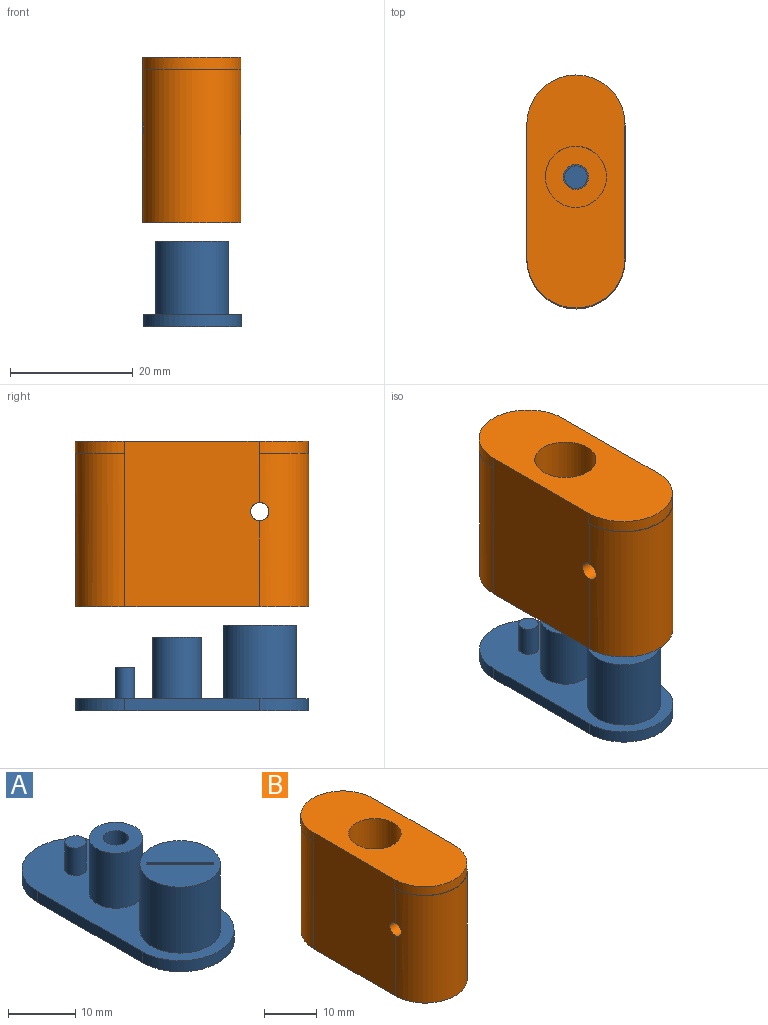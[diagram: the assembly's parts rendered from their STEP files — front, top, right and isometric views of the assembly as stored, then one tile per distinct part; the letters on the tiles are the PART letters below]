
ASSEMBLY  parts=2 mates=1
PART A: 19 faces, bbox 16x38x14 mm
  f0: plane 12x0.35mm, normal (0.71,-0.71,0), area 6mm2, adj f1,f4,f5,f6
  f1: plane 12x7.07mm, normal (-0.71,-0.71,0), area 120mm2, adj f0,f2,f5,f6
  f2: plane 12x0.35mm, normal (-0.71,0.71,0), area 6mm2, adj f1,f4,f5,f6
  f3: cylinder r=6mm len=12mm, axis (0,0,-1), area 452.4mm2, adj f5,f7
  f4: plane 12x7.07mm, normal (0.71,0.71,0), area 120mm2, adj f0,f2,f5,f6
  f5: plane 12x12mm, normal (0,0,1), area 108.1mm2, adj f0,f1,f2,f3,f4
  f6: plane 7.42x7.42mm, normal (0,0,1), area 5mm2, adj f0,f1,f2,f4
  f7: plane 38x16mm, normal (0,0,1), area 381.7mm2, adj f3,f9,f12,f13,f14,f15,f17
  f8: cylinder r=1.85mm len=10mm, axis (0,0,-1), area 116.2mm2, adj f10,f18
  f9: cylinder r=4mm len=10mm, axis (0,0,-1), area 251.3mm2, adj f7,f10
  f10: plane 8x8mm, normal (0,0,1), area 39.5mm2, adj f8,f9
  f11: plane 38x16mm, normal (0,0,-1), area 553.1mm2, adj f12,f13,f14,f15
  f12: cylinder r=8mm len=16mm, axis (0,0,1), area 50.3mm2, adj f7,f11,f13,f15
  f13: plane 22x2mm, normal (-1,0,0), area 44mm2, adj f7,f11,f12,f14
  f14: cylinder r=8mm len=16mm, axis (0,0,1), area 50.3mm2, adj f7,f11,f13,f15
  f15: plane 22x2mm, normal (1,0,0), area 44mm2, adj f7,f11,f12,f14
  f16: plane 3.2x3.2mm, normal (0,0,1), area 8mm2, adj f17
  f17: cylinder r=1.6mm len=5mm, axis (0,0,-1), area 50.3mm2, adj f7,f16
  f18: plane 3.7x3.7mm, normal (0,0,1), area 10.8mm2, adj f8
PART B: 26 faces, bbox 16.6x38.7x27.6 mm
  f0: cylinder r=8mm len=25mm, axis (0,0,-1), area 621.2mm2, adj f3,f5,f7,f10,f24,f25
  f1: plane 13x13mm, normal (0,0,-1), area 121.7mm2, adj f2,f19,f20,f21,f22
  f2: cylinder r=6.5mm len=13mm, axis (0,0,-1), area 494.6mm2, adj f1,f10
  f3: plane 16.01x8.01mm, normal (0,0,1), area 1.8mm2, adj f0,f16
  f4: cylinder r=5mm len=10mm, axis (0,0,-1), area 314.2mm2, adj f10,f13
  f5: plane 27x22.12mm, normal (1,0,0), area 590.5mm2, adj f0,f6,f10,f15,f16,f17,f25
  f6: cylinder r=8mm len=25mm, axis (0,0,-1), area 628.3mm2, adj f5,f7,f10,f14
  f7: plane 27x22.12mm, normal (-1,0,0), area 590.5mm2, adj f0,f6,f10,f15,f16,f17,f24
  f8: cylinder r=2.4mm len=25mm, axis (0,0,-1), area 377mm2, adj f10,f18
  f9: cylinder r=5mm len=15mm, axis (0,0,-1), area 471.2mm2, adj f12,f15
  f10: plane 38x16mm, normal (0,0,-1), area 323.7mm2, adj f0,f2,f4,f5,f6,f7,f8
  f11: cylinder r=2.05mm len=4.1mm, axis (0,0,-1), area 25.8mm2, adj f12,f13
  f12: plane 10x10mm, normal (0,0,1), area 65.3mm2, adj f9,f11
  f13: plane 10x10mm, normal (0,0,-1), area 65.3mm2, adj f4,f11
  f14: plane 16.01x8.01mm, normal (0,0,-1), area 1.8mm2, adj f6,f17
  f15: plane 38x16mm, normal (0,0,1), area 474.5mm2, adj f5,f7,f9,f16,f17
  f16: cylinder r=8mm len=16mm, axis (0,0,-1), area 50.3mm2, adj f3,f5,f7,f15
  f17: cylinder r=8mm len=16mm, axis (0,0,-1), area 50.3mm2, adj f5,f7,f14,f15
  f18: plane 4.8x4.8mm, normal (0,0,-1), area 18.1mm2, adj f8
  f19: plane 12.66x0.71mm, normal (0.71,-0.71,0), area 12.7mm2, adj f1,f21,f22,f23
  f20: plane 12.66x0.71mm, normal (-0.71,0.71,0), area 12.7mm2, adj f1,f21,f22,f23
  f21: plane 13.29x8.41mm, normal (-0.71,-0.71,0), area 129.2mm2, adj f1,f19,f20,f23,f25
  f22: plane 13.29x8.41mm, normal (0.71,0.71,0), area 129.2mm2, adj f1,f19,f20,f23,f24
  f23: plane 8.49x8.49mm, normal (0,0,-1), area 11mm2, adj f19,f20,f21,f22
  f24: cylinder r=1.5mm len=8.8mm, axis (-1,0,0), area 69.2mm2, adj f0,f7,f22
  f25: cylinder r=1.5mm len=8.79mm, axis (-1,0,0), area 68.3mm2, adj f0,f5,f21
PLACE A t=(-7.54,5.57,-15.78)mm
PLACE B t=(-7.54,5.57,-0.78)mm
MATE slider A.f9 <-> B.f4  axis (0,0,1) through (-7.54,8.07,-5.78)mm
